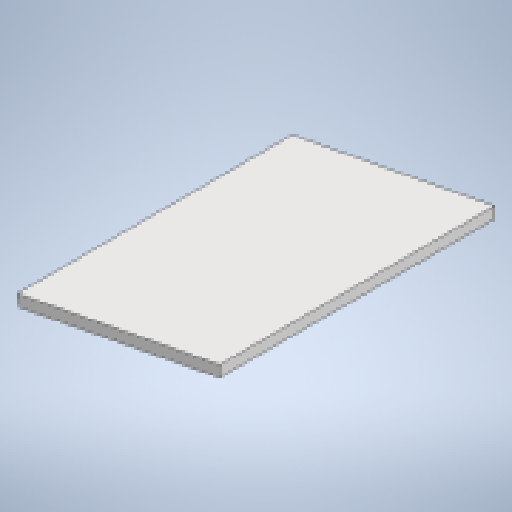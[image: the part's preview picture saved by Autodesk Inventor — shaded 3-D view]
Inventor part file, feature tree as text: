
AUTODESK INVENTOR PART (.ipt)
format: ipt  version: 2023.5 (Build 275446000, 446)  size: 149,504 bytes
history: native  units: mm
features: reference x11, other x7, extrude x2, sketch x2
ambient origin geometry x8: Origin, YZ Plane, XZ Plane, XY Plane, X Axis, Y Axis, Z Axis, Center Point
bodies: Body1 (feature_tree)
feature tree (22):
  other  "Bryła1"
  extrude  "Wyciągnięcie proste1"  Depth=2.0mm
  extrude  "Wyciągnięcie proste2"  Depth=50.0mm TaperAngle=0.0deg
  sketch  "Szkic1"
  reference  "Odniesienie1"
  sketch  "Szkic2"
  reference  "Odniesienie2"
  reference  "Odniesienie3"
  reference  "Odniesienie4"
  reference  "Odniesienie5"
  reference  "Odniesienie6"
  reference  "Odniesienie7"
  reference  "Odniesienie8"
  reference  "Odniesienie9"
  reference  "Odniesienie10"
  reference  "Odniesienie11"
  parser-record x1  (decoder bookkeeping rows leaked as tree rows — omitted from the tree; the rows remain in map.json)
  other  "stratos_v2_mechanics.iam"
  other  "wymiar:1"
  other  "MikroSumo:1"
  other  "scianka_prawa:1"
  other  "montaz_osi:1"
note: 1 file-system path scrubbed to <path> (originals preserved in map.json)
